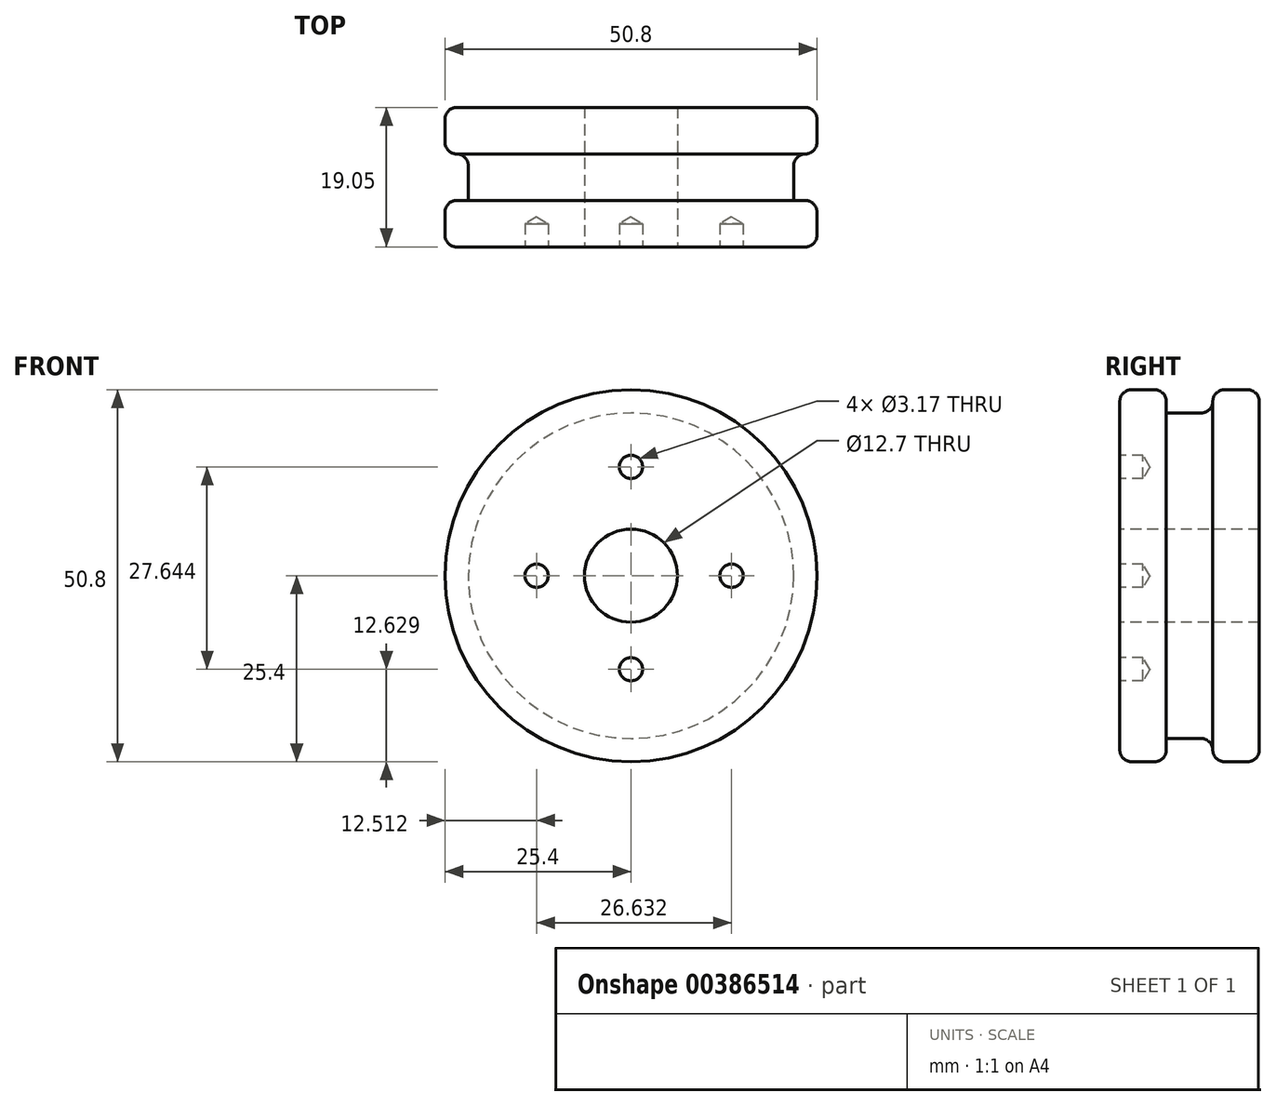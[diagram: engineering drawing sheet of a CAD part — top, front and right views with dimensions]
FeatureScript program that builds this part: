
annotation { "Feature Type Name" : "Feature", "Feature Type Description" : "" }
export const myFeature = defineFeature(function(context is Context, id is Id, definition is map)
    precondition{}
    {
        {
            var Q0;
            Q0=qCreatedBy(makeId("Front.planeOp"),FACE);
            var sketch = newSketch(context, id + "F0", { "sketchPlane" : qUnion([Q0])});
            skCircle(sketch, "E0", {"center": v(0, 0) * mm, "radius": 25.4 * mm});
            skSolve(sketch);
        }
        {
            var Q0;
            Q0=makeQuery(id+"F0.imprint","IMPRINT",FACE,{"disambiguationData":[TD([[makeQuery(id+"F0.imprint","IMPRINT",EDGE,{"derivedFrom":sQuery(id+"F0.wireOp",EDGE,"E0")}),1.0]])]});
            extrude(context, id + "F1", {"entities" : qUnion([Q0]), "depth" : 6.35 * mm});
        }
        {
            var Q0;
            Q0=qCreatedBy(makeId("Front.planeOp"),FACE);
            var sketch = newSketch(context, id + "F2", { "sketchPlane" : qUnion([Q0])});
            skCircle(sketch, "E1", {"center": v(0, 0) * mm, "radius": 22.22 * mm});
            skSolve(sketch);
        }
        {
            var Q0;
            Q0 = qSketchRegion(id + "F2", true);
            extrude(context, id + "F3", {"entities" : qUnion([Q0]), "operationType" : NewBodyOperationType.ADD, "depth" : 12.7 * mm});
        }
        {
            var Q0;
            Q0=makeQuery(id+"F3.opExtrude","CAP_FACE",FACE,{"disambiguationData":[OSD([sQuery(id+"F2.wireOp",EDGE,"E1")])],"isStart":false});
            var sketch = newSketch(context, id + "F4", { "sketchPlane" : qUnion([Q0])});
            skCircle(sketch, "E2", {"center": v(0, 0) * mm, "radius": 25.4 * mm});
            skSolve(sketch);
        }
        {
            var Q0;
            Q0=makeQuery(id+"F4.imprint","IMPRINT",FACE,{"disambiguationData":[TD([[makeQuery(id+"F4.imprint","IMPRINT",EDGE,{"derivedFrom":sQuery(id+"F4.wireOp",EDGE,"E2")}),1.0]])]});
            var Q1;
            Q1=makeQuery(id+"F4.imprint","IMPRINT",FACE,{"disambiguationData":[TD([[makeQuery(id+"F4.imprint","IMPRINT",EDGE,{"derivedFrom":makeQuery(id+"F3.opExtrude","CAP_EDGE",EDGE,{"disambiguationData":[OSD([sQuery(id+"F2.wireOp",EDGE,"E1")])],"isStart":false})}),1.0]])]});
            extrude(context, id + "F5", {"entities" : qUnion([Q0, Q1]), "operationType" : NewBodyOperationType.ADD, "depth" : 6.35 * mm});
        }
        {
            var Q0;
            Q0=makeQuery(id+"F5.opExtrude","CAP_FACE",FACE,{"disambiguationData":[OSD([sQuery(id+"F4.wireOp",EDGE,"E2")])],"isStart":false});
            var sketch = newSketch(context, id + "F6", { "sketchPlane" : qUnion([Q0])});
            skPoint(sketch, "E3", {"position": v(0, 0) * mm});
            skPoint(sketch, "E4", {"position": v(0, 14.87) * mm});
            skPoint(sketch, "E5", {"position": v(13.74, 0) * mm});
            skPoint(sketch, "E6", {"position": v(0, -12.77) * mm});
            skPoint(sketch, "E7", {"position": v(-12.89, 0) * mm});
            skSolve(sketch);
        }
        {
            var Q0;
            Q0=sQuery(id+"F6.wireOp",VERTEX,"E4");
            var Q1;
            Q1=sQuery(id+"F6.wireOp",VERTEX,"E5");
            var Q2;
            Q2=sQuery(id+"F6.wireOp",VERTEX,"E6");
            var Q3;
            Q3=sQuery(id+"F6.wireOp",VERTEX,"E7");
            var Q4;
            Q4=makeQuery(id+"F1.opExtrude","SWEPT_BODY",BODY,{"disambiguationData":[OSD([sQuery(id+"F0.wireOp",EDGE,"E0")])]});
            hole(context, id + "F7", {"style" : HoleStyle.SIMPLE, "endStyle" : HoleEndStyle.BLIND, "holeDiameter" : 3.17 * mm, "holeDepth" : 3.17 * mm, "isTappedThrough" : true, "tappedDepth" : 12.7 * mm, "tapClearance" : 3, "locations" : qUnion([Q0, Q1, Q2, Q3]), "scope" : qUnion([Q4])});
        }
        {
            var Q0;
            Q0=sQuery(id+"F6.wireOp",VERTEX,"E3");
            var Q1;
            Q1=makeQuery(id+"F1.opExtrude","SWEPT_BODY",BODY,{"disambiguationData":[OSD([sQuery(id+"F0.wireOp",EDGE,"E0")])]});
            hole(context, id + "F8", {"style" : HoleStyle.SIMPLE, "endStyle" : HoleEndStyle.THROUGH, "holeDiameter" : 12.7 * mm, "isTappedThrough" : true, "tappedDepth" : 12.7 * mm, "tapClearance" : 3, "locations" : qUnion([Q0]), "scope" : qUnion([Q1])});
        }
        {
            var Q0;
            Q0=makeQuery(id+"F1.opExtrude","CAP_EDGE",EDGE,{"disambiguationData":[OSD([sQuery(id+"F0.wireOp",EDGE,"E0")])],"isStart":true});
            var Q1;
            Q1=makeQuery(id+"F1.opExtrude","CAP_EDGE",EDGE,{"disambiguationData":[OSD([sQuery(id+"F0.wireOp",EDGE,"E0")])],"isStart":false});
            var Q2;
            Q2=makeQuery(id+"F3.boolean.opBoolean","INTERSECT",EDGE,{"derivedFrom":[makeQuery(id+"F1.opExtrude","CAP_FACE",FACE,{"disambiguationData":[OSD([sQuery(id+"F0.wireOp",EDGE,"E0")])],"isStart":false}),makeQuery(id+"F3.opExtrude","SWEPT_FACE",FACE,{"disambiguationData":[OSD([sQuery(id+"F2.wireOp",EDGE,"E1")])]})]});
            var Q3;
            Q3=makeQuery(id+"F3.opExtrude","CAP_EDGE",EDGE,{"disambiguationData":[OSD([sQuery(id+"F2.wireOp",EDGE,"E1")])],"isStart":false});
            var Q4;
            Q4=makeQuery(id+"F5.opExtrude","CAP_EDGE",EDGE,{"disambiguationData":[OSD([sQuery(id+"F4.wireOp",EDGE,"E2")])],"isStart":true});
            var Q5;
            Q5=makeQuery(id+"F5.opExtrude","CAP_EDGE",EDGE,{"disambiguationData":[OSD([sQuery(id+"F4.wireOp",EDGE,"E2")])],"isStart":false});
            fillet(context, id + "F9", {"entities" : qUnion([Q0, Q1, Q2, Q3, Q4, Q5]), "radius" : 1.59 * mm, "tangentPropagation" : true, "allowEdgeOverflow" : false});
        }
    });
